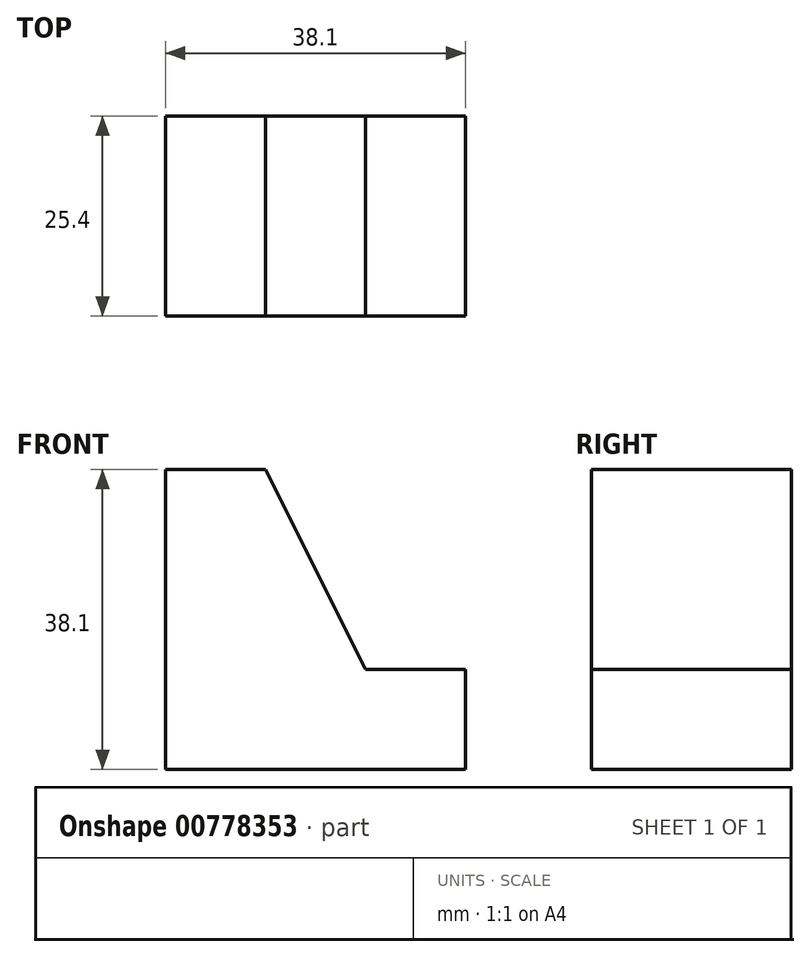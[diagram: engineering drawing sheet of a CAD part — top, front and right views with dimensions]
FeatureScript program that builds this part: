
annotation { "Feature Type Name" : "Feature", "Feature Type Description" : "" }
export const myFeature = defineFeature(function(context is Context, id is Id, definition is map)
    precondition{}
    {
        {
            var Q0;
            Q0=qCreatedBy(makeId("Front.planeOp"),FACE);
            var sketch = newSketch(context, id + "F0", { "sketchPlane" : qUnion([Q0])});
            skLineSegment(sketch, "E0", {"start": v(0, 0) * mm, "end": v(38.1, 0) * mm});
            skLineSegment(sketch, "E1", {"start": v(38.1, 0) * mm, "end": v(38.1, 12.7) * mm});
            skLineSegment(sketch, "E2", {"start": v(38.1, 12.7) * mm, "end": v(25.4, 12.7) * mm});
            skLineSegment(sketch, "E3", {"start": v(0, 0) * mm, "end": v(0, 38.1) * mm});
            skLineSegment(sketch, "E4", {"start": v(0, 38.1) * mm, "end": v(12.7, 38.1) * mm});
            skLineSegment(sketch, "E5", {"start": v(12.7, 38.1) * mm, "end": v(25.4, 12.7) * mm});
            skSolve(sketch);
        }
        {
            var Q0;
            Q0 = qSketchRegion(id + "F0", true);
            extrude(context, id + "F1", {"entities" : qUnion([Q0]), "depth" : 25.4 * mm, "offsetDistance" : 25.4 * mm});
        }
    });
